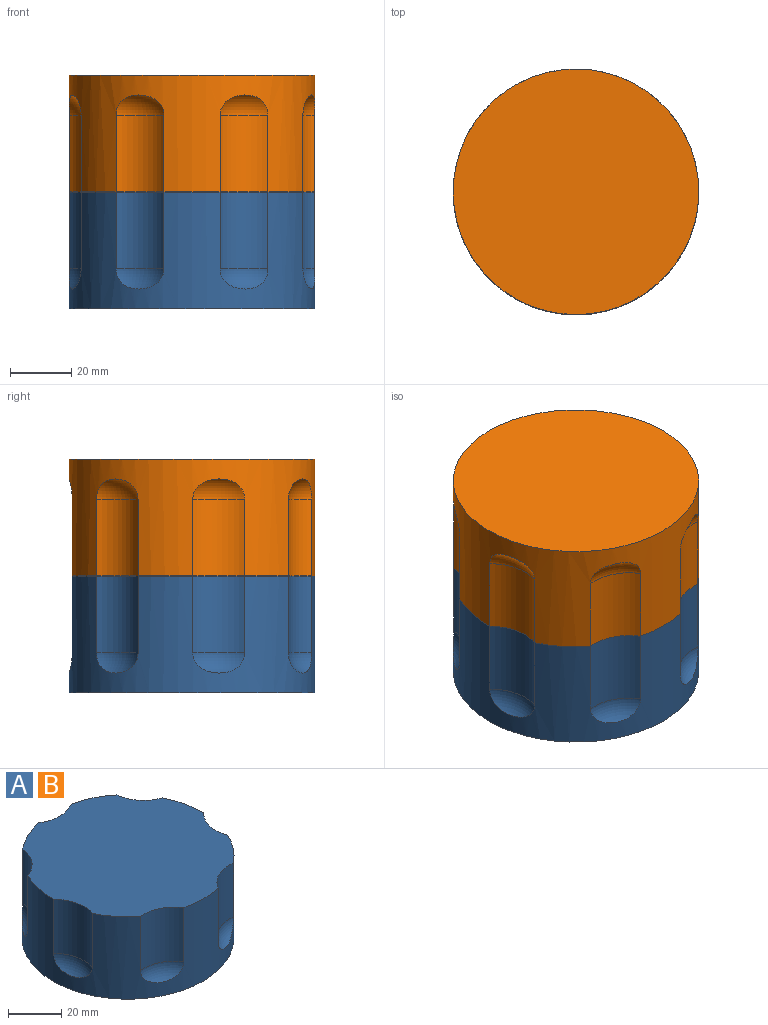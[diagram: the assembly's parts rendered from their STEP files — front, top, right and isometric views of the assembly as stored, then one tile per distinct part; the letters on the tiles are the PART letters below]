
ASSEMBLY  parts=2 mates=1
PART A: 17 faces, bbox 91.2x88.9x38 mm
  f0: cylinder r=16mm len=25mm, axis (0,0,1), area 457.9mm2, adj f6,f9,f10
  f1: cylinder r=16mm len=25mm, axis (0,0,1), area 457.9mm2, adj f6,f9,f11
  f2: cylinder r=16mm len=25mm, axis (0,0,1), area 457.9mm2, adj f6,f9,f12
  f3: cylinder r=16mm len=25mm, axis (0,0,1), area 457.9mm2, adj f6,f9,f13
  f4: cylinder r=16mm len=25mm, axis (0,0,1), area 457.9mm2, adj f6,f9,f14
  f5: cylinder r=16mm len=25mm, axis (0,0,1), area 457.9mm2, adj f6,f9,f15
  f6: cylinder r=40mm len=80mm, axis (0,0,-1), area 5845.5mm2, adj f0,f1,f2,f3,f4,f5,f7,f8
  f7: plane 80x80mm, normal (0,0,-1), area 5026.5mm2, adj f6
  f8: cylinder r=16mm len=25mm, axis (0,0,1), area 457.9mm2, adj f6,f9,f16
  f9: plane 80x79.05mm, normal (0,0,1), area 4739.7mm2, adj f0,f1,f2,f3,f4,f5,f6,f8
  f10: torus R=8mm, axis (0,0,1), area 107.9mm2, adj f0,f6
  f11: torus R=8mm, axis (0,0,1), area 107.9mm2, adj f1,f6
  f12: torus R=8mm, axis (0,0,1), area 107.9mm2, adj f2,f6
  f13: torus R=8mm, axis (0,0,1), area 107.9mm2, adj f3,f6
  f14: torus R=8mm, axis (0,0,1), area 107.9mm2, adj f4,f6
  f15: torus R=8mm, axis (0,0,1), area 107.9mm2, adj f5,f6
  f16: torus R=8mm, axis (0,0,1), area 107.9mm2, adj f6,f8
PART B: same geometry as A
PLACE A t=(-105.84,-52.85,-23.12)mm
PLACE B rot(axis=(0,1,0),180deg) t=(-105.84,-52.85,52.88)mm
MATE fastened B.f6 <-> A.f6  axis (0,0,-1) through (-105.84,-52.85,14.88)mm
